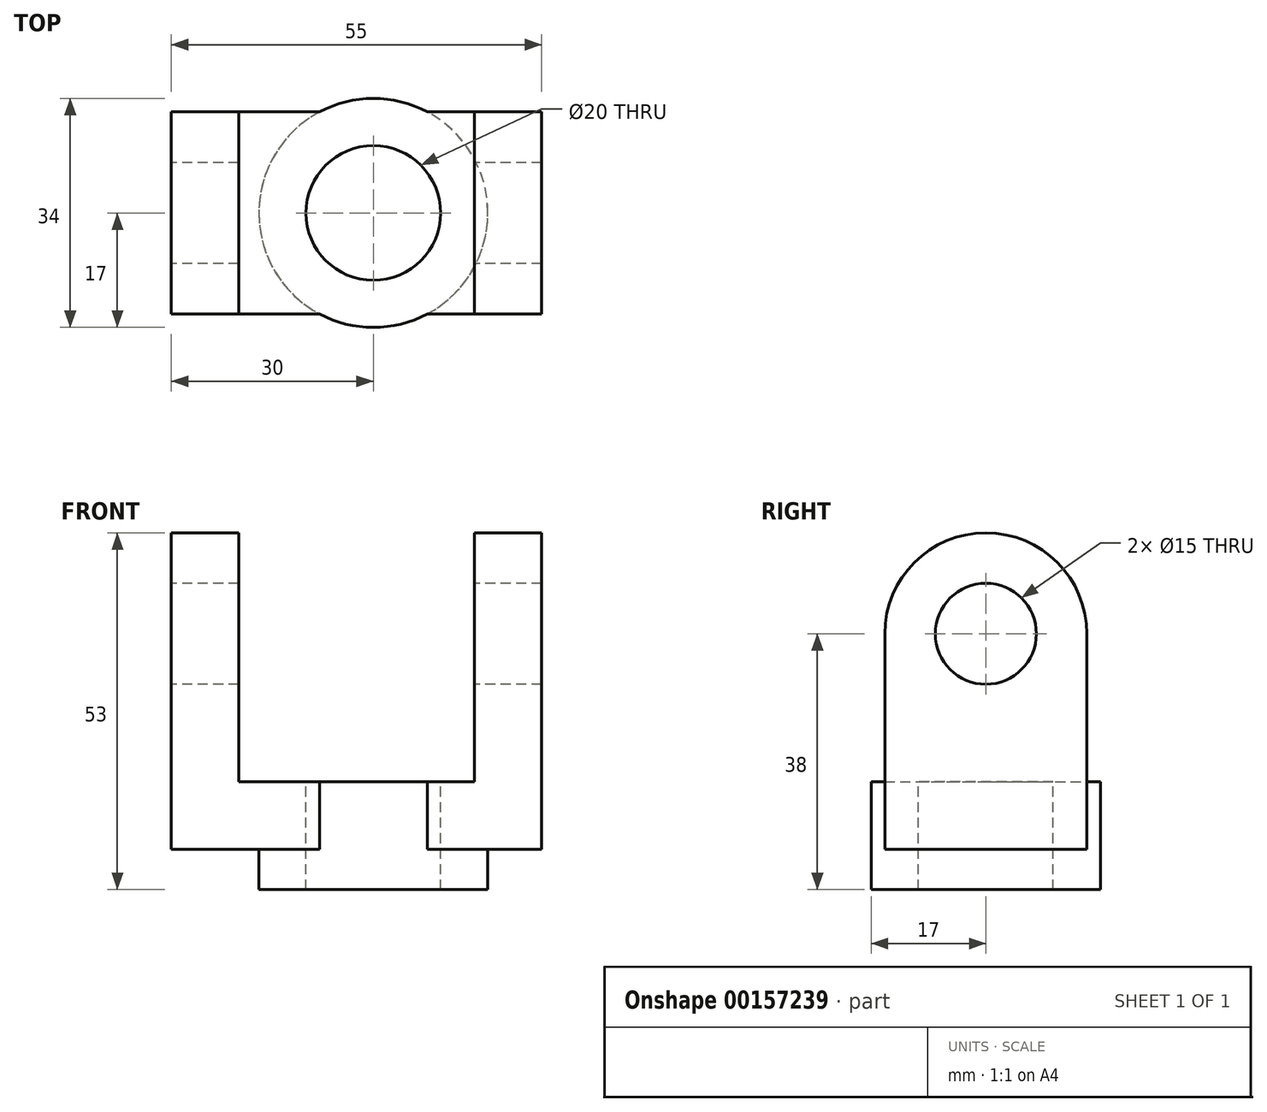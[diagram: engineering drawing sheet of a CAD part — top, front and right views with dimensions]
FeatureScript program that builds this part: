
annotation { "Feature Type Name" : "Feature", "Feature Type Description" : "" }
export const myFeature = defineFeature(function(context is Context, id is Id, definition is map)
    precondition{}
    {
        {
            var Q0;
            Q0=qCreatedBy(makeId("Front.planeOp"),FACE);
            var sketch = newSketch(context, id + "F0", { "sketchPlane" : qUnion([Q0])});
            skLineSegment(sketch, "E0", {"start": v(0, 0) * mm, "end": v(55, 0) * mm});
            skLineSegment(sketch, "E1", {"start": v(0, 0) * mm, "end": v(0, 47) * mm});
            skLineSegment(sketch, "E2", {"start": v(0, 47) * mm, "end": v(10, 47) * mm});
            skLineSegment(sketch, "E3", {"start": v(10, 47) * mm, "end": v(10, 10) * mm});
            skLineSegment(sketch, "E4", {"start": v(10, 10) * mm, "end": v(45, 10) * mm});
            skLineSegment(sketch, "E5", {"start": v(45, 10) * mm, "end": v(45, 47) * mm});
            skLineSegment(sketch, "E6", {"start": v(45, 47) * mm, "end": v(55, 47) * mm});
            skLineSegment(sketch, "E7", {"start": v(55, 47) * mm, "end": v(55, 0) * mm});
            skSolve(sketch);
        }
        {
            var Q0;
            Q0 = qSketchRegion(id + "F0", true);
            extrude(context, id + "F1", {"entities" : qUnion([Q0]), "depth" : 30 * mm});
        }
        {
            var Q0;
            Q0=qCreatedBy(makeId("Top.planeOp"),FACE);
            var sketch = newSketch(context, id + "F2", { "sketchPlane" : qUnion([Q0])});
            skCircle(sketch, "E8", {"center": v(30, -15) * mm, "radius": 17 * mm});
            skSolve(sketch);
        }
        {
            var Q0;
            Q0 = qSketchRegion(id + "F2", true);
            extrude(context, id + "F3", {"entities" : qUnion([Q0]), "operationType" : NewBodyOperationType.ADD, "depth" : (10) * mm, "hasSecondDirection" : true, "secondDirectionOppositeDirection" : true, "secondDirectionDepth" : 6 * mm});
        }
        {
            var Q0;
            Q0=qCreatedBy(makeId("Top.planeOp"),FACE);
            var sketch = newSketch(context, id + "F4", { "sketchPlane" : qUnion([Q0])});
            skCircle(sketch, "E9", {"center": v(30, -15) * mm, "radius": 10 * mm});
            skSolve(sketch);
        }
        {
            var Q0;
            Q0 = qSketchRegion(id + "F4", true);
            extrude(context, id + "F5", {"entities" : qUnion([Q0]), "operationType" : NewBodyOperationType.REMOVE, "oppositeDirection" : true, "depth" : 25 * mm, "hasSecondDirection" : true, "secondDirectionOppositeDirection" : false, "secondDirectionDepth" : 25 * mm});
        }
        {
            var Q0;
            Q0=qCreatedBy(makeId("Right.planeOp"),FACE);
            var sketch = newSketch(context, id + "F6", { "sketchPlane" : qUnion([Q0])});
            skLineSegment(sketch, "E10", {"start": v(0, 0) * mm, "end": v(0, 32) * mm, "construction": true});
            skLineSegment(sketch, "E11", {"start": v(0, 32) * mm, "end": v(-30, 32) * mm, "construction": true});
            skLineSegment(sketch, "E12", {"start": v(-30, 32) * mm, "end": v(-30, 0) * mm, "construction": true});
            skLineSegment(sketch, "E13", {"start": v(-30, 0) * mm, "end": v(0, 0) * mm, "construction": true});
            skArc(sketch, "E14", {"start": v(0, 32) * mm, "mid": v(-15, 47) * mm, "end": v(-30, 32) * mm});
            skLineSegment(sketch, "E15", {"start": v(-30, 32) * mm, "end": v(-30, 47) * mm});
            skLineSegment(sketch, "E16", {"start": v(-30, 47) * mm, "end": v(0, 47) * mm});
            skPoint(sketch, "E16.endSnap0", {"position": v(-15, 47) * mm});
            skLineSegment(sketch, "E17", {"start": v(0, 47) * mm, "end": v(0, 32) * mm});
            skCircle(sketch, "E18", {"center": v(-15, 32) * mm, "radius": 7.5 * mm});
            skSolve(sketch);
        }
        {
            var Q0;
            Q0 = qSketchRegion(id + "F6", true);
            extrude(context, id + "F7", {"entities" : qUnion([Q0]), "operationType" : NewBodyOperationType.REMOVE, "depth" : 70 * mm});
        }
    });
